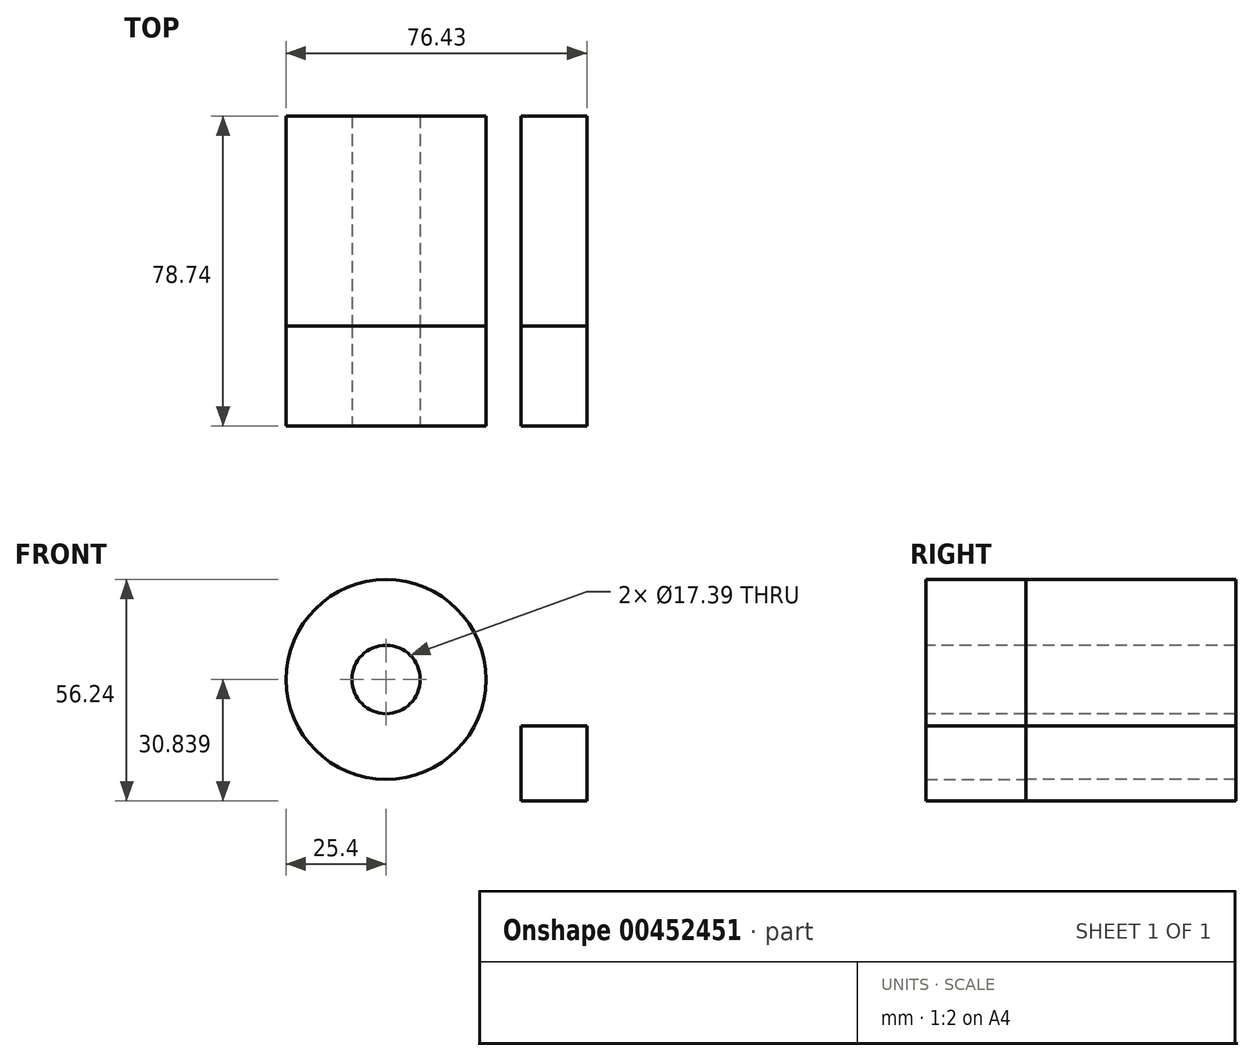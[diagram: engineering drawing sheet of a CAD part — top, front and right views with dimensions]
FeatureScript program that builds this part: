
annotation { "Feature Type Name" : "Feature", "Feature Type Description" : "" }
export const myFeature = defineFeature(function(context is Context, id is Id, definition is map)
    precondition{}
    {
        {
            var Q0;
            Q0=qCreatedBy(makeId("Front.planeOp"),FACE);
            var sketch = newSketch(context, id + "F0", { "sketchPlane" : qUnion([Q0])});
            skCircle(sketch, "E0", {"center": v(-55.7, 43.47) * mm, "radius": 25.4 * mm});
            skLineSegment(sketch, "E1", {"start": v(-43.4, 9.65) * mm, "end": v(18.5, 9.65) * mm});
            skLineSegment(sketch, "E2.bottom", {"start": v(-21.44, 31.69) * mm, "end": v(-4.68, 31.69) * mm});
            skLineSegment(sketch, "E2.top", {"start": v(-21.44, 12.63) * mm, "end": v(-4.68, 12.63) * mm});
            skLineSegment(sketch, "E2.left", {"start": v(-21.44, 31.69) * mm, "end": v(-21.44, 12.63) * mm});
            skLineSegment(sketch, "E2.right", {"start": v(-4.68, 31.69) * mm, "end": v(-4.68, 12.63) * mm});
            skSolve(sketch);
        }
        {
            var Q0;
            Q0 = qSketchRegion(id + "F0", true);
            extrude(context, id + "F1", {"entities" : qUnion([Q0]), "oppositeDirection" : true, "depth" : 53.34 * mm});
        }
        {
            var Q0;
            Q0 = qSketchRegion(id + "F0", true);
            var Q1;
            Q1=makeQuery(id+"F1.opExtrude","CAP_FACE",FACE,{"disambiguationData":[OSD([sQuery(id+"F0.wireOp",EDGE,"E2.bottom"),sQuery(id+"F0.wireOp",EDGE,"E2.top"),sQuery(id+"F0.wireOp",EDGE,"E2.left"),sQuery(id+"F0.wireOp",EDGE,"E2.right")])],"isStart":true});
            extrude(context, id + "F2", {"entities" : qUnion([Q0, Q1]), "depth" : 25.4 * mm});
        }
        {
            var Q0;
            Q0=makeQuery(id+"F2.opExtrude","CAP_FACE",FACE,{"disambiguationData":[OSD([sQuery(id+"F0.wireOp",EDGE,"E0")])],"isStart":false});
            var sketch = newSketch(context, id + "F3", { "sketchPlane" : qUnion([Q0])});
            skCircle(sketch, "E3", {"center": v(-55.7, 43.47) * mm, "radius": 8.7 * mm});
            skSolve(sketch);
        }
        {
            var Q0;
            Q0 = qSketchRegion(id + "F3", true);
            extrude(context, id + "F4", {"entities" : qUnion([Q0]), "operationType" : NewBodyOperationType.REMOVE, "endBound" : BoundingType.THROUGH_ALL, "oppositeDirection" : true, "depth" : 25.4 * mm});
        }
    });
